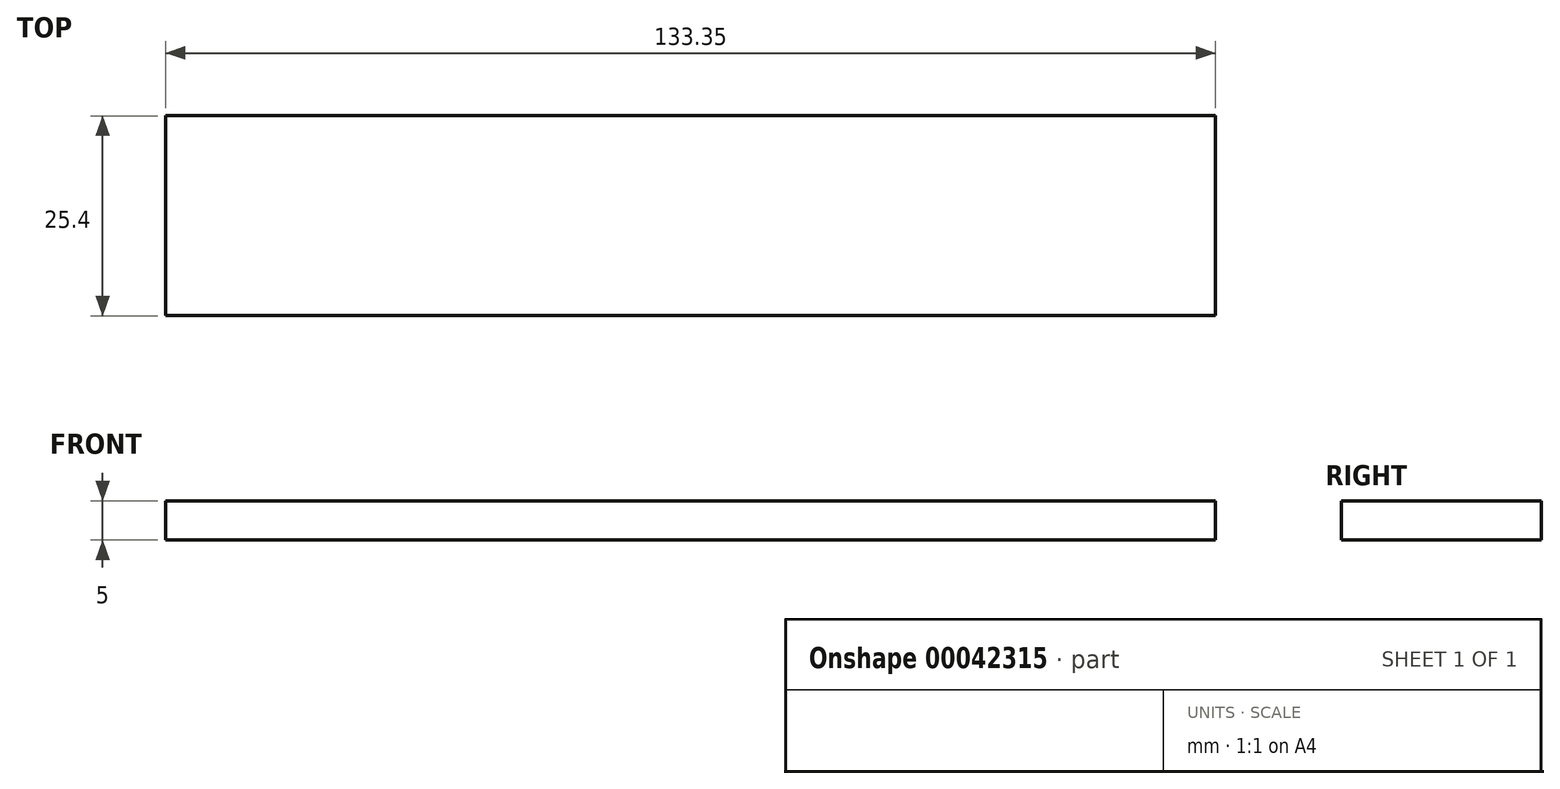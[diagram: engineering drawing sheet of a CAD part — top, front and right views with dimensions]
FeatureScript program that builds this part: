
annotation { "Feature Type Name" : "Feature", "Feature Type Description" : "" }
export const myFeature = defineFeature(function(context is Context, id is Id, definition is map)
    precondition{}
    {
        {
            var Q0;
            Q0=qCreatedBy(makeId("Top.planeOp"),FACE);
            var sketch = newSketch(context, id + "F0", { "sketchPlane" : qUnion([Q0])});
            skLineSegment(sketch, "E0.bottom", {"start": v(-43.48, 65.96) * mm, "end": v(89.87, 65.96) * mm});
            skLineSegment(sketch, "E0.top", {"start": v(-43.48, -41.99) * mm, "end": v(89.87, -41.99) * mm});
            skLineSegment(sketch, "E0.left", {"start": v(-43.48, 65.96) * mm, "end": v(-43.48, -41.99) * mm});
            skLineSegment(sketch, "E0.right", {"start": v(89.87, 65.96) * mm, "end": v(89.87, -41.99) * mm});
            skLineSegment(sketch, "E1.0", {"start": v(-40.3, 62.79) * mm, "end": v(86.7, 62.79) * mm});
            skLineSegment(sketch, "E1.1", {"start": v(-40.3, 62.79) * mm, "end": v(-40.3, -38.81) * mm});
            skLineSegment(sketch, "E1.2", {"start": v(-40.3, -38.81) * mm, "end": v(86.7, -38.81) * mm});
            skLineSegment(sketch, "E1.3", {"start": v(86.7, 62.79) * mm, "end": v(86.7, -38.81) * mm});
            skLineSegment(sketch, "E2", {"start": v(-43.48, -16.59) * mm, "end": v(89.87, -16.59) * mm});
            skSolve(sketch);
        }
        {
            var Q0;
            {var subQ8=sQuery(id+"F0.wireOp",EDGE,"E0.top");Q0=makeQuery(id+"F0.imprint","IMPRINT",FACE,{"disambiguationData":[TD([[makeQuery(id+"F0.imprint","IMPRINT",EDGE,{"derivedFrom":subQ8}),1.0]])]});}
            var Q1;
            {var subQ5=sQuery(id+"F0.wireOp",EDGE,"E1.2");Q1=makeQuery(id+"F0.imprint","IMPRINT",FACE,{"disambiguationData":[TD([[makeQuery(id+"F0.imprint","IMPRINT",EDGE,{"derivedFrom":subQ5}),1.0]])]});}
            extrude(context, id + "F1", {"entities" : qUnion([Q0, Q1]), "depth" : 5 * mm});
        }
    });
